# Revit family: Mixing_Valve-Leonard_Valve_Company-Megatron-NV_200_LF_2PS-1
name_source: partatom
category: Pipe Accessories
revit_build: Autodesk Revit 2015 (Build: 20140606_1530(x64)
units: mm (PartAtom-declared; Revit-internal decimal feet)

## types (1)
- NV-200-LF-2PS
    BIMobject category = Valves
    Brand url = http://www.leonardvalve.com
    Description = The Nucleus Digitally Controlled Mixing Valve from Leonard Valve Company serves as the central monitor & control of a Domestic Hot Water System. The Nucleus Digitally Controlled Mixing Valve capabilities include:

+/- 2°F Mixed Water Temperature in accordance with ASSE 1017-2009.
+/- 2°F Mixed Water Temperature during periods of low or no system demand
0.5 GPM Minimum Flow with Continuously Operating Recirculation Pump
Automatic Shutoff of Valve upon Cold or Hot Supply Failure
System Setup & Commissioning from Nucleus Control Module–no PC or Laptop Required
LCD Display & Sensor Indicators – Set Point Temperature & Actual Temperature
BMS Interface – Native Support for Six Different Protocols including BACnet & Modbus
Ethernet Connection for PC or LAN for Valve Programming or Interrogation
Web Server to remotely monitor & control Nucleus Mixing Valve
Data Logger – stores up to 30 days of temperatures, pressure & flows
Nucleus is UL Listed & Approved to E484833. Eco-Mix Certified Lead Free Construction
    Design country = United States
    Edition number = 1
    IFC Classification = Valve
    Manufacturer = Leonard Valve Company
    Manufacturer country = United States
    Manufacturer name = Leonard Valve Company
    Model = NV-200-LF-2PS
    Nominal height = 0 "
    Nominal width = 0 "
    OmniClass Code = 23-27 31 29
    OmniClass Description = Mixing Valves
    Pipe Material = Bronze-Leonard_Valve_Company
    Pipe Radius .625 = 0.6879 "
    Pipe Radius 1.0 = 1.0625 "
    Pipe Radius 2.0 = 2.0625 "
    Product SKU = nv-200-lf-2ps
    Product data url = https://www.bimobject.com
    Product family = Mixing Valves for Liquid Services
    Product group = Digitally Controlled Mixing Valves
    Product url = http://www.leonardvalvecompany.com
    QR code = https://www.bimobject.com
    UNSPSC Code = 401416
    URL = http://www.leonardvalve.com
    Valve Box Material = Steel-Leonard_Valve-Baked_White
    Weight Net (Kg) = 0

## geometry (parser evidence)
native form markers: Sweep x48
no freeform markers — native parametric forms only
